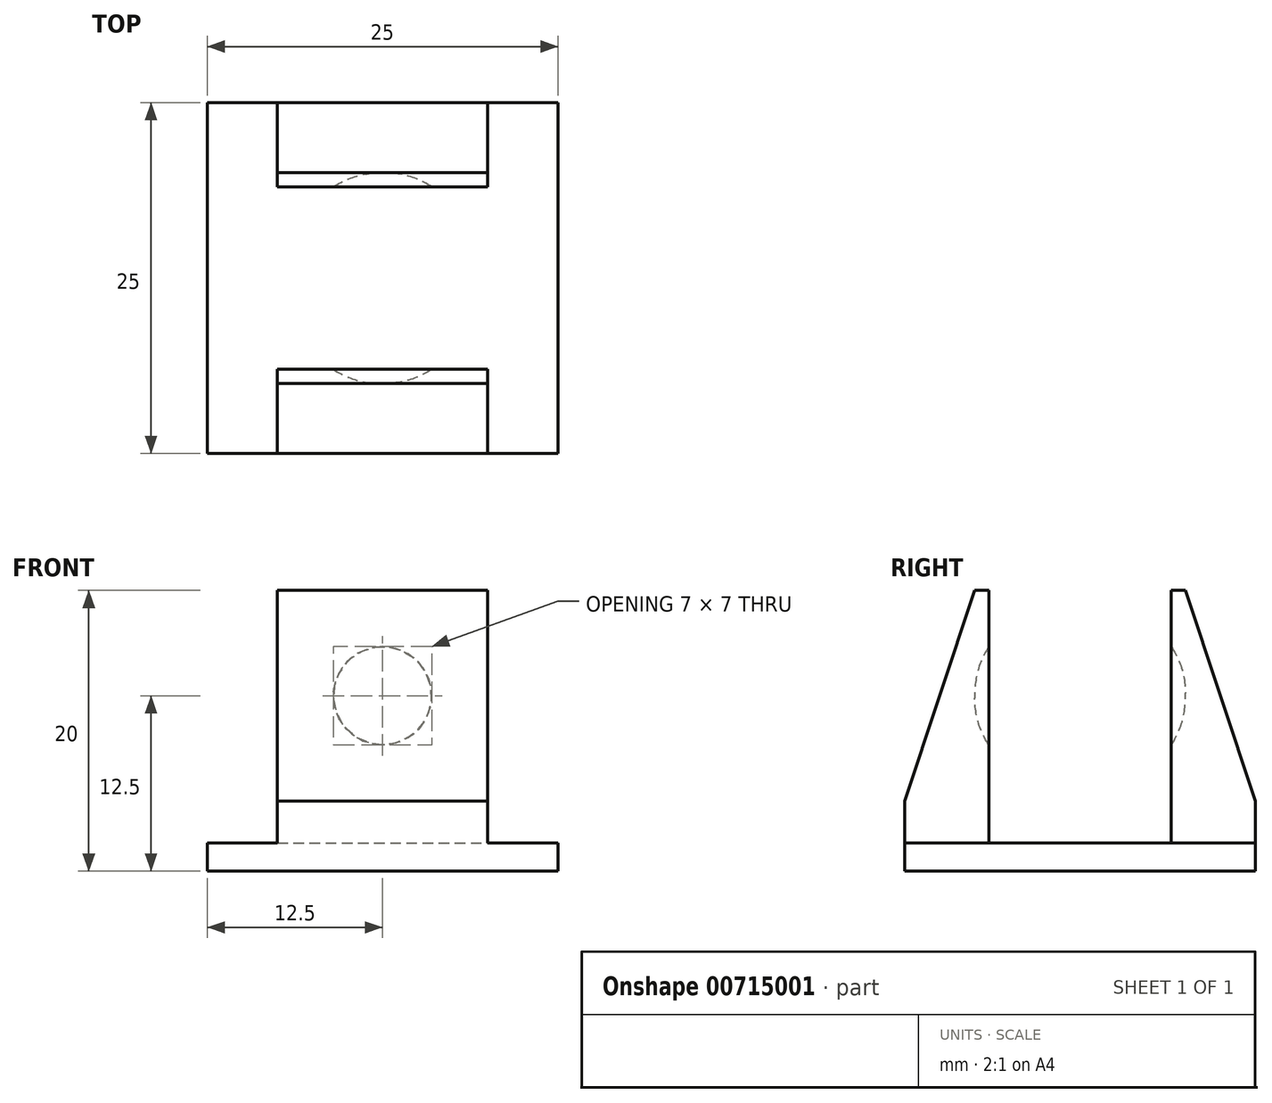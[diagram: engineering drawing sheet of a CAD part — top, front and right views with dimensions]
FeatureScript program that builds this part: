
annotation { "Feature Type Name" : "Feature", "Feature Type Description" : "" }
export const myFeature = defineFeature(function(context is Context, id is Id, definition is map)
    precondition{}
    {
        {
            var Q0;
            Q0=qCreatedBy(makeId("Top.planeOp"),FACE);
            var sketch = newSketch(context, id + "F0", { "sketchPlane" : qUnion([Q0])});
            skLineSegment(sketch, "E0.bottom", {"start": v(12.5, 12.5) * mm, "end": v(-12.5, 12.5) * mm});
            skLineSegment(sketch, "E0.top", {"start": v(12.5, -12.5) * mm, "end": v(-12.5, -12.5) * mm});
            skLineSegment(sketch, "E0.left", {"start": v(12.5, 12.5) * mm, "end": v(12.5, -12.5) * mm});
            skLineSegment(sketch, "E0.right", {"start": v(-12.5, 12.5) * mm, "end": v(-12.5, -12.5) * mm});
            skPoint(sketch, "E0.middle", {"position": v(0, 0) * mm});
            skSolve(sketch);
        }
        {
            var Q0;
            Q0=makeQuery(id+"F0.imprint","IMPRINT",FACE,{"disambiguationData":[TD([[makeQuery(id+"F0.imprint","IMPRINT",EDGE,{"derivedFrom":sQuery(id+"F0.wireOp",EDGE,"E0.bottom")}),1.0]])]});
            extrude(context, id + "F1", {"entities" : qUnion([Q0]), "depth" : 2 * mm, "offsetDistance" : 25 * mm});
        }
        {
            var Q0;
            Q0=makeQuery(id+"F1.opExtrude","CAP_FACE",FACE,{"disambiguationData":[OSD([sQuery(id+"F0.wireOp",EDGE,"E0.bottom"),sQuery(id+"F0.wireOp",EDGE,"E0.top"),sQuery(id+"F0.wireOp",EDGE,"E0.left"),sQuery(id+"F0.wireOp",EDGE,"E0.right")])],"isStart":false});
            var sketch = newSketch(context, id + "F2", { "sketchPlane" : qUnion([Q0])});
            skPoint(sketch, "E1.middle", {"position": v(0, 0) * mm});
            skLineSegment(sketch, "E2.bottom", {"start": v(7.5, 12.5) * mm, "end": v(-7.5, 12.5) * mm, "construction": true});
            skLineSegment(sketch, "E2.top", {"start": v(7.5, -12.5) * mm, "end": v(-7.5, -12.5) * mm, "construction": true});
            skLineSegment(sketch, "E2.left", {"start": v(7.5, 12.5) * mm, "end": v(7.5, -12.5) * mm, "construction": true});
            skLineSegment(sketch, "E2.right", {"start": v(-7.5, 12.5) * mm, "end": v(-7.5, -12.5) * mm, "construction": true});
            skLineSegment(sketch, "E3.bottom", {"start": v(-7.5, -12.5) * mm, "end": v(7.5, -12.5) * mm});
            skLineSegment(sketch, "E3.top", {"start": v(-7.5, -6.5) * mm, "end": v(7.5, -6.5) * mm});
            skLineSegment(sketch, "E3.left", {"start": v(-7.5, -12.5) * mm, "end": v(-7.5, -6.5) * mm});
            skLineSegment(sketch, "E3.right", {"start": v(7.5, -12.5) * mm, "end": v(7.5, -6.5) * mm});
            skLineSegment(sketch, "E4.bottom", {"start": v(-7.5, 12.5) * mm, "end": v(7.5, 12.5) * mm});
            skLineSegment(sketch, "E4.top", {"start": v(-7.5, 6.5) * mm, "end": v(7.5, 6.5) * mm});
            skLineSegment(sketch, "E4.left", {"start": v(-7.5, 12.5) * mm, "end": v(-7.5, 6.5) * mm});
            skLineSegment(sketch, "E4.right", {"start": v(7.5, 12.5) * mm, "end": v(7.5, 6.5) * mm});
            skSolve(sketch);
        }
        {
            var Q0;
            Q0 = qSketchRegion(id + "F2", true);
            extrude(context, id + "F3", {"entities" : qUnion([Q0]), "operationType" : NewBodyOperationType.ADD, "depth" : 18 * mm, "offsetDistance" : 25 * mm});
        }
        {
            var Q0;
            Q0=makeQuery(id+"F3.opExtrude","SWEPT_FACE",FACE,{"disambiguationData":[OSD([sQuery(id+"F2.wireOp",EDGE,"E4.top")])]});
            var sketch = newSketch(context, id + "F4", { "sketchPlane" : qUnion([Q0])});
            skLineSegment(sketch, "E5.bottom", {"start": v(-7.5, 20) * mm, "end": v(7.5, 20) * mm, "construction": true});
            skLineSegment(sketch, "E5.top", {"start": v(-7.5, 12.5) * mm, "end": v(7.5, 12.5) * mm, "construction": true});
            skLineSegment(sketch, "E5.left", {"start": v(-7.5, 20) * mm, "end": v(-7.5, 12.5) * mm, "construction": true});
            skLineSegment(sketch, "E5.right", {"start": v(7.5, 20) * mm, "end": v(7.5, 12.5) * mm, "construction": true});
            skCircle(sketch, "E6", {"center": v(0, 12.5) * mm, "radius": 3.5 * mm});
            skSolve(sketch);
        }
        {
            var Q0;
            Q0=makeQuery(id+"F4.imprint","IMPRINT",FACE,{"disambiguationData":[TD([[makeQuery(id+"F4.imprint","IMPRINT",EDGE,{"derivedFrom":sQuery(id+"F4.wireOp",EDGE,"E6")}),1.0]])]});
            extrude(context, id + "F5", {"entities" : qUnion([Q0]), "operationType" : NewBodyOperationType.REMOVE, "oppositeDirection" : true, "depth" : 1 * mm, "offsetDistance" : 25 * mm});
        }
        {
            var Q0;
            Q0=makeQuery(id+"F3.opExtrude","SWEPT_FACE",FACE,{"disambiguationData":[OSD([sQuery(id+"F2.wireOp",EDGE,"E3.top")])]});
            var sketch = newSketch(context, id + "F6", { "sketchPlane" : qUnion([Q0])});
            skLineSegment(sketch, "E7.bottom", {"start": v(-7.5, 20) * mm, "end": v(7.5, 20) * mm, "construction": true});
            skLineSegment(sketch, "E7.top", {"start": v(-7.5, 12.5) * mm, "end": v(7.5, 12.5) * mm, "construction": true});
            skLineSegment(sketch, "E7.left", {"start": v(-7.5, 20) * mm, "end": v(-7.5, 12.5) * mm, "construction": true});
            skLineSegment(sketch, "E7.right", {"start": v(7.5, 20) * mm, "end": v(7.5, 12.5) * mm, "construction": true});
            skCircle(sketch, "E8", {"center": v(0, 12.5) * mm, "radius": 3.5 * mm});
            skSolve(sketch);
        }
        {
            var Q0;
            Q0=makeQuery(id+"F6.imprint","IMPRINT",FACE,{"disambiguationData":[TD([[makeQuery(id+"F6.imprint","IMPRINT",EDGE,{"derivedFrom":sQuery(id+"F6.wireOp",EDGE,"E8")}),1.0]])]});
            extrude(context, id + "F7", {"entities" : qUnion([Q0]), "operationType" : NewBodyOperationType.REMOVE, "oppositeDirection" : true, "depth" : 1 * mm, "offsetDistance" : 25 * mm});
        }
        {
            var Q0;
            Q0=makeQuery(id+"F5.boolean.opBoolean","COPY",EDGE,{"derivedFrom":makeQuery(id+"F5.opExtrude","CAP_EDGE",EDGE,{"disambiguationData":[OSD([sQuery(id+"F4.wireOp",EDGE,"E6")])],"isStart":false})});
            var Q1;
            Q1=makeQuery(id+"F7.boolean.opBoolean","COPY",EDGE,{"derivedFrom":makeQuery(id+"F7.opExtrude","CAP_EDGE",EDGE,{"disambiguationData":[OSD([sQuery(id+"F6.wireOp",EDGE,"E8")])],"isStart":false})});
            fillet(context, id + "F8", {"entities" : qUnion([Q0, Q1]), "radius" : 6 * mm, "tangentPropagation" : true, "rho" : 0.5, "crossSection" : FilletCrossSection.CONIC, "allowEdgeOverflow" : false});
        }
        {
            var Q0;
            Q0=makeQuery(id+"F3.opExtrude","CAP_EDGE",EDGE,{"disambiguationData":[OSD([sQuery(id+"F2.wireOp",EDGE,"E3.bottom")])],"isStart":false});
            chamfer(context, id + "F9", {"entities" : qUnion([Q0]), "chamferType" : ChamferType.TWO_OFFSETS, "width1" : 15 * mm, "oppositeDirection" : false, "width2" : 5 * mm, "tangentPropagation" : true});
        }
        {
            var Q0;
            Q0=makeQuery(id+"F3.opExtrude","CAP_EDGE",EDGE,{"disambiguationData":[OSD([sQuery(id+"F2.wireOp",EDGE,"E4.bottom")])],"isStart":false});
            chamfer(context, id + "F10", {"entities" : qUnion([Q0]), "chamferType" : ChamferType.TWO_OFFSETS, "width1" : 5 * mm, "oppositeDirection" : false, "width2" : 15 * mm, "tangentPropagation" : true});
        }
    });
